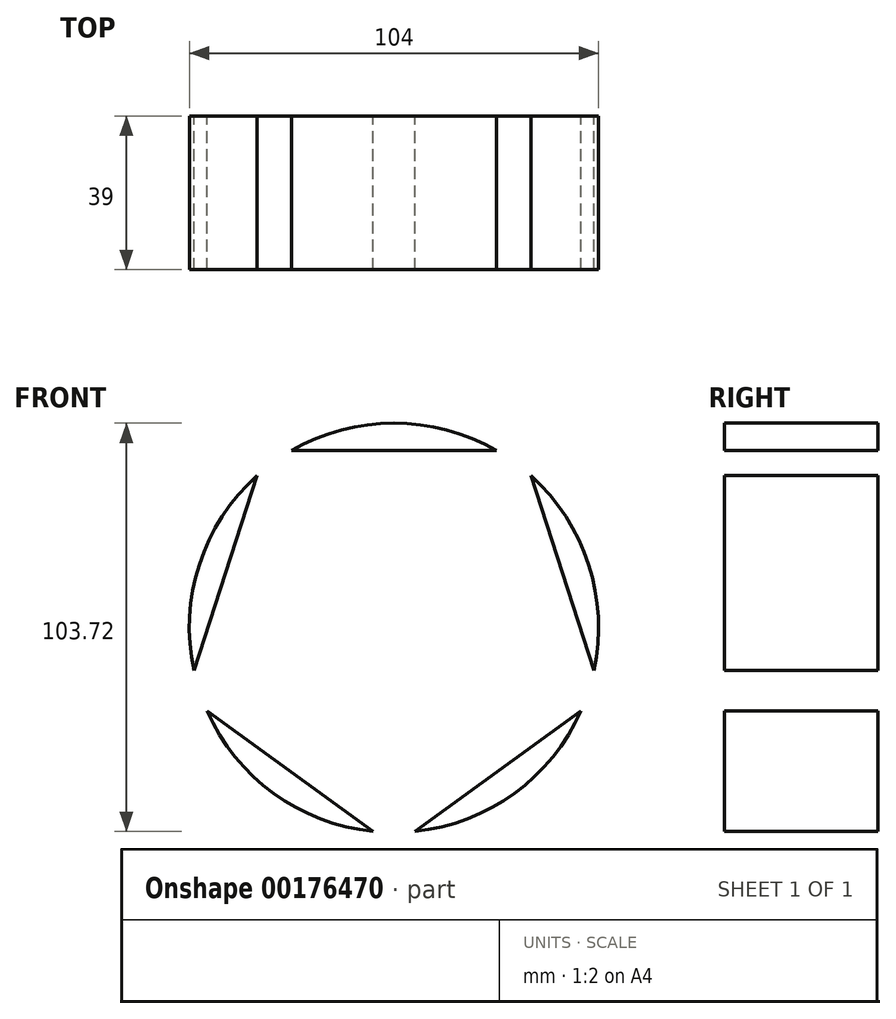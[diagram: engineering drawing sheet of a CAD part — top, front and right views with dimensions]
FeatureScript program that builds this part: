
annotation { "Feature Type Name" : "Feature", "Feature Type Description" : "" }
export const myFeature = defineFeature(function(context is Context, id is Id, definition is map)
    precondition{}
    {
        {
            var Q0;
            Q0=qCreatedBy(makeId("Front.planeOp"),FACE);
            var sketch = newSketch(context, id + "F0", { "sketchPlane" : qUnion([Q0])});
            skCircle(sketch, "E0", {"center": v(0, 0) * mm, "radius": 75 * mm, "construction": true});
            skCircle(sketch, "E1.cCircle", {"center": v(0, 0) * mm, "radius": 45 * mm, "construction": true});
            skLineSegment(sketch, "E1.0", {"start": v(-32.7, 45) * mm, "end": v(32.7, 45) * mm});
            skLineSegment(sketch, "E1.1", {"start": v(32.7, 45) * mm, "end": v(52.9, -17.19) * mm});
            skLineSegment(sketch, "E1.2", {"start": v(52.9, -17.19) * mm, "end": v(0, -55.62) * mm});
            skLineSegment(sketch, "E1.3", {"start": v(0, -55.62) * mm, "end": v(-52.9, -17.19) * mm});
            skLineSegment(sketch, "E1.4", {"start": v(-52.9, -17.19) * mm, "end": v(-32.7, 45) * mm});
            skPoint(sketch, "E1.0.midPoint", {"position": v(0, 45) * mm});
            skLineSegment(sketch, "E2", {"start": v(26.45, -36.4) * mm, "end": v(-32.7, 45) * mm, "construction": true});
            skCircle(sketch, "E3", {"center": v(0, 0) * mm, "radius": 52 * mm});
            skArc(sketch, "E4", {"start": v(-65.91, -35.79) * mm, "mid": v(0, 75) * mm, "end": v(65.91, -35.79) * mm});
            skPoint(sketch, "E5", {"position": v(0, -55.62) * mm});
            skArc(sketch, "E6", {"start": v(34.75, 38.69) * mm, "mid": v(32.7, 45) * mm, "end": v(26.06, 45) * mm});
            skArc(sketch, "E7", {"start": v(-26.06, 45) * mm, "mid": v(-32.7, 45) * mm, "end": v(-34.75, 38.69) * mm});
            skArc(sketch, "E8", {"start": v(-50.85, -10.88) * mm, "mid": v(-52.9, -17.19) * mm, "end": v(-47.53, -21.09) * mm});
            skArc(sketch, "E9", {"start": v(47.53, -21.09) * mm, "mid": v(52.9, -17.19) * mm, "end": v(50.85, -10.88) * mm});
            skLineSegment(sketch, "E10", {"start": v(0, -52) * mm, "end": v(0, -52) * mm});
            skArc(sketch, "E11", {"start": v(-5.37, -51.72) * mm, "mid": v(0, -55.62) * mm, "end": v(5.37, -51.72) * mm});
            skLineSegment(sketch, "E12", {"start": v(0, 45) * mm, "end": v(0, -187.88) * mm, "construction": true});
            skPoint(sketch, "E13", {"position": v(0, -125) * mm});
            skLineSegment(sketch, "E14", {"start": v(0, -187.88) * mm, "end": v(-62.5, -187.88) * mm, "construction": true});
            skLineSegment(sketch, "E15", {"start": v(0, -187.88) * mm, "end": v(62.5, -187.88) * mm, "construction": true});
            skPoint(sketch, "E16", {"position": v(0, -175) * mm});
            skLineSegment(sketch, "E17", {"start": v(0, -175) * mm, "end": v(-62.5, -175) * mm, "construction": true});
            skLineSegment(sketch, "E18", {"start": v(0, -175) * mm, "end": v(62.5, -175) * mm, "construction": true});
            skPoint(sketch, "E19", {"position": v(0, -155) * mm});
            skLineSegment(sketch, "E20", {"start": v(0, -155) * mm, "end": v(-37.5, -155) * mm, "construction": true});
            skArc(sketch, "E21", {"start": v(-62.5, -187.88) * mm, "mid": v(0, -198) * mm, "end": v(62.5, -187.88) * mm});
            skLineSegment(sketch, "E22", {"start": v(0, -198) * mm, "end": v(131.81, -198) * mm, "construction": true});
            skArc(sketch, "E23", {"start": v(-62.5, -175) * mm, "mid": v(-65, -181.44) * mm, "end": v(-62.5, -187.88) * mm});
            skLineSegment(sketch, "E24", {"start": v(-65, -227.56) * mm, "end": v(-65, -146.64) * mm, "construction": true});
            skArc(sketch, "E25.MirrorCS", {"start": v(62.5, -175) * mm, "mid": v(65, -181.44) * mm, "end": v(62.5, -187.88) * mm});
            skPoint(sketch, "E26", {"position": v(0, -157.18) * mm});
            skLineSegment(sketch, "E27.MirrorCS", {"start": v(-27, -107.46) * mm, "end": v(-65.91, -35.79) * mm});
            skArc(sketch, "E28.MirrorCS", {"start": v(27, -107.46) * mm, "mid": v(23.23, -132.51) * mm, "end": v(36.43, -154.14) * mm});
            skPoint(sketch, "E29.orphan", {"position": v(36.43, -154.14) * mm});
            skArc(sketch, "E30.MirrorCS", {"start": v(-27, -107.46) * mm, "mid": v(-23.23, -132.51) * mm, "end": v(-36.43, -154.14) * mm});
            skPoint(sketch, "E31", {"position": v(27, -107.46) * mm});
            skPoint(sketch, "E32", {"position": v(-27, -107.46) * mm});
            skLineSegment(sketch, "E33.trimOffspring", {"start": v(27, -107.46) * mm, "end": v(65.91, -35.79) * mm});
            skLineSegment(sketch, "E34", {"start": v(0, -157.18) * mm, "end": v(27, -107.46) * mm, "construction": true});
            skLineSegment(sketch, "E35", {"start": v(0, -157.18) * mm, "end": v(-27, -107.46) * mm, "construction": true});
            skLineSegment(sketch, "E36", {"start": v(22.5, -125) * mm, "end": v(-22.5, -125) * mm, "construction": true});
            skLineSegment(sketch, "E37", {"start": v(-22.5, -144.13) * mm, "end": v(-22.5, -125) * mm, "construction": true});
            skLineSegment(sketch, "E38", {"start": v(-62.5, -175) * mm, "end": v(-36.43, -154.14) * mm});
            skLineSegment(sketch, "E39.MirrorCS", {"start": v(62.5, -175) * mm, "end": v(36.43, -154.14) * mm});
            skSolve(sketch);
        }
        {
            var Q0;
            Q0=makeQuery(id+"F0.imprint","IMPRINT",FACE,{"disambiguationData":[TD([[makeQuery(id+"F0.imprint","IMPRINT",EDGE,{"derivedFrom":sQuery(id+"F0.wireOp",EDGE,"E4")}),-1.0]])]});
            var Q1;
            {var subQ0=sQuery(id+"F0.wireOp",EDGE,"E3");var subQ1=sQuery(id+"F0.wireOp",EDGE,"E1.3");var subQ2=makeQuery(id+"F0.imprint","INTERSECT",VERTEX,{"derivedFrom":[subQ1,subQ0,sQuery(id+"F0.wireOp",EDGE,"E8")]});Q1=makeQuery(id+"F0.imprint","IMPRINT",FACE,{"disambiguationData":[TD([[makeQuery(id+"F0.imprint","IMPRINT",EDGE,{"disambiguationData":[TD([[subQ2,1.0]])],"derivedFrom":subQ1}),1.0]])]});}
            var Q2;
            {var subQ0=sQuery(id+"F0.wireOp",EDGE,"E3");var subQ1=sQuery(id+"F0.wireOp",EDGE,"E1.2");var subQ2=makeQuery(id+"F0.imprint","INTERSECT",VERTEX,{"derivedFrom":[subQ1,subQ0,sQuery(id+"F0.wireOp",EDGE,"E9")]});Q2=makeQuery(id+"F0.imprint","IMPRINT",FACE,{"disambiguationData":[TD([[makeQuery(id+"F0.imprint","IMPRINT",EDGE,{"disambiguationData":[TD([[subQ2,-1.0]])],"derivedFrom":subQ1}),1.0]])]});}
            var Q3;
            {var subQ0=sQuery(id+"F0.wireOp",EDGE,"E3");var subQ1=sQuery(id+"F0.wireOp",EDGE,"E1.1");var subQ2=makeQuery(id+"F0.imprint","INTERSECT",VERTEX,{"derivedFrom":[subQ1,subQ0,sQuery(id+"F0.wireOp",EDGE,"E6")]});Q3=makeQuery(id+"F0.imprint","IMPRINT",FACE,{"disambiguationData":[TD([[makeQuery(id+"F0.imprint","IMPRINT",EDGE,{"disambiguationData":[TD([[subQ2,-1.0]])],"derivedFrom":subQ1}),1.0]])]});}
            var Q4;
            {var subQ0=sQuery(id+"F0.wireOp",EDGE,"E3");var subQ1=sQuery(id+"F0.wireOp",EDGE,"E1.0");var subQ2=makeQuery(id+"F0.imprint","INTERSECT",VERTEX,{"derivedFrom":[subQ1,subQ0,sQuery(id+"F0.wireOp",EDGE,"E6")]});Q4=makeQuery(id+"F0.imprint","IMPRINT",FACE,{"disambiguationData":[TD([[makeQuery(id+"F0.imprint","IMPRINT",EDGE,{"disambiguationData":[TD([[subQ2,1.0]])],"derivedFrom":subQ1}),1.0]])]});}
            var Q5;
            {var subQ0=sQuery(id+"F0.wireOp",EDGE,"E3");var subQ1=sQuery(id+"F0.wireOp",EDGE,"E1.4");var subQ2=makeQuery(id+"F0.imprint","INTERSECT",VERTEX,{"derivedFrom":[subQ1,subQ0,sQuery(id+"F0.wireOp",EDGE,"E7")]});Q5=makeQuery(id+"F0.imprint","IMPRINT",FACE,{"disambiguationData":[TD([[makeQuery(id+"F0.imprint","IMPRINT",EDGE,{"disambiguationData":[TD([[subQ2,1.0]])],"derivedFrom":subQ1}),1.0]])]});}
            extrude(context, id + "F1", {"entities" : qUnion([Q0, Q1, Q2, Q3, Q4, Q5]), "depth" : 39 * mm});
        }
    });
